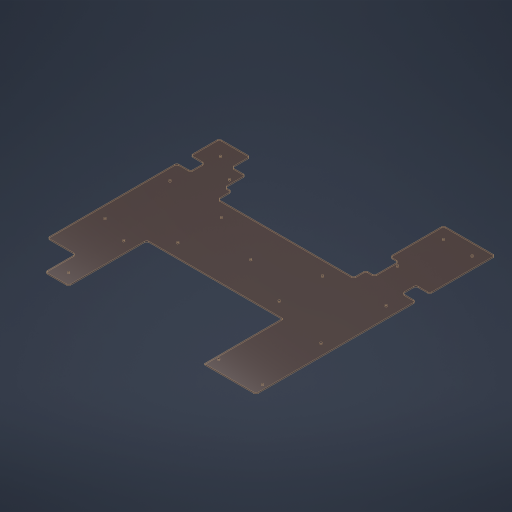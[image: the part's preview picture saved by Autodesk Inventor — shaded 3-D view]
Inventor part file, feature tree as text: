
AUTODESK INVENTOR PART (.ipt)
format: ipt  version: 2023.4 (Build 274418000, 418)  size: 403,968 bytes
history: native  units: in
note: dims shown in document units (in); Inventor stores cm internally (conversion verified against a paired STEP export)
features: sketch x4, extrude x3, projected_geometry x3, fillet x2, hole x1
ambient origin geometry x8: Origin, YZ Plane, XZ Plane, XY Plane, X Axis, Y Axis, Z Axis, Center Point
bodies: Solid1 (feature_tree)
feature tree (13):
  extrude  "Extrusion1"  Depth=25.97in
  extrude  "Extrusion2"  Depth=9.75in
  fillet  "Fillet1"  Radius=14.75in
  hole  "Hole1"  [1 undecoded]
  extrude  "Extrusion4"  Depth=0.1875in
  fillet  "Fillet2"  Radius=2.1255in
  sketch  "Sketch1"  dims[d0=25.97in d1=25.97in]
  sketch  "Sketch2"  dims[d3=8.5in d4=9.75in d5=14.75in]
  sketch  "Sketch4"  dims[d6=0.125in d7=0.0in d8=0.225in]
  sketch  "Sketch5"  dims[d9=2.75in d10=1.831in d11=2.1255in d12=4.0in d14=0.0in d15=0.0in d16=0.75in d17=18.125in d18=1.5in d19=1.5in d20=2.5in d21=2.5in d28=1.5in d29=1.25in d30=4.75in d31=2.25in d32=2.0in d33=4.75in d34=1.25in d35=1.25in d36=1.25in d37=1.25in d38=1.25in d39=2.0in d40=1.875in d41=1.5in d42=1.5in d43=1.875in d44=1.25in d47=1.25in d48=1.25in d49=1.25in d50=2.0in d51=1.25in d52=0.201in d53=0.75in d54=0.385in d55=0.25in d56=0.5635in d57=0.12in d58=0.0in d59=5.0in d60=1.25in d61=4.0in d62=2.75in d63=1.5869in d64=1.3213in d65=0.375in d66=0.375in d67=0.0in d68=0.0in d69=0.225in d70=0.75in d71=2.25in d72=0.1875in]
  projected_geometry  "Project Cut Edges1"
  projected_geometry  "Project Cut Edges3"
  projected_geometry  "Project Cut Edges4"
note: 1 required parameter value undecoded (feature->parameter linkage not recoverable at this tier; creation-order binding heuristic only, values carry confidence <= 0.55)
